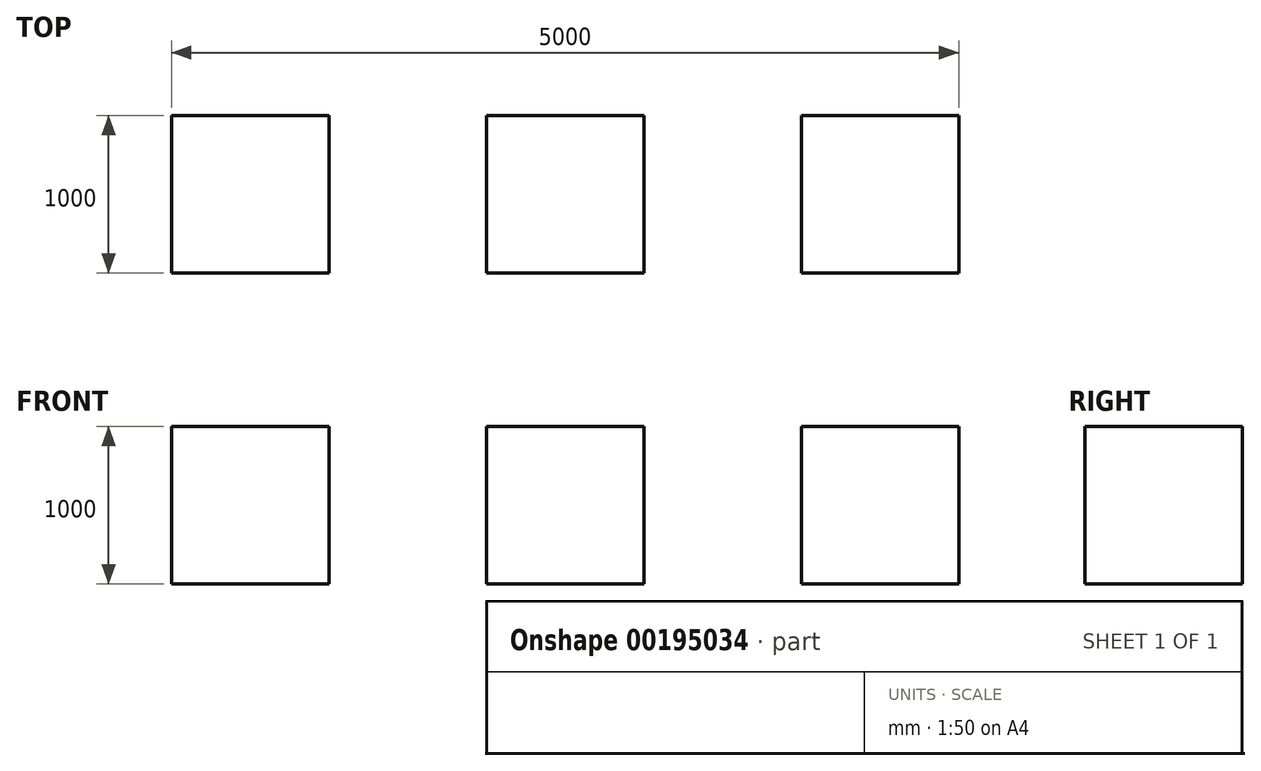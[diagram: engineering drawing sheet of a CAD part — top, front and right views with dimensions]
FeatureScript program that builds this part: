
annotation { "Feature Type Name" : "Feature", "Feature Type Description" : "" }
export const myFeature = defineFeature(function(context is Context, id is Id, definition is map)
    precondition{}
    {
        {
            var Q0;
            Q0=qCreatedBy(makeId("Top.planeOp"),FACE);
            var sketch = newSketch(context, id + "F0", { "sketchPlane" : qUnion([Q0])});
            skLineSegment(sketch, "E0.bottom", {"start": v(500, 500) * mm, "end": v(-500, 500) * mm});
            skLineSegment(sketch, "E0.top", {"start": v(500, -500) * mm, "end": v(-500, -500) * mm});
            skLineSegment(sketch, "E0.left", {"start": v(500, 500) * mm, "end": v(500, -500) * mm});
            skLineSegment(sketch, "E0.right", {"start": v(-500, 500) * mm, "end": v(-500, -500) * mm});
            skPoint(sketch, "E0.middle", {"position": v(0, 0) * mm});
            skSolve(sketch);
        }
        {
            var Q0;
            Q0 = qSketchRegion(id + "F0", true);
            extrude(context, id + "F1", {"entities" : qUnion([Q0]), "endBound" : BoundingType.SYMMETRIC, "depth" : 1000 * mm});
        }
        {
            var Q0;
            Q0=makeQuery(id+"F1.opExtrude","SWEPT_BODY",BODY,{"disambiguationData":[OSD([sQuery(id+"F0.wireOp",EDGE,"E0.bottom"),sQuery(id+"F0.wireOp",EDGE,"E0.top"),sQuery(id+"F0.wireOp",EDGE,"E0.left"),sQuery(id+"F0.wireOp",EDGE,"E0.right")])]});
            transform(context, id + "F2", {"entities" : qUnion([Q0]), "transformType" : TransformType.TRANSLATION_3D, "dx" : 2000 * mm, "dy" : 0 * mm, "dz" : 0 * mm, "makeCopy" : true});
        }
        {
            var Q0;
            Q0=makeQuery(id+"F2.opPattern","COPY",BODY,{"derivedFrom":makeQuery(id+"F1.opExtrude","SWEPT_BODY",BODY,{"disambiguationData":[OSD([sQuery(id+"F0.wireOp",EDGE,"E0.bottom"),sQuery(id+"F0.wireOp",EDGE,"E0.top"),sQuery(id+"F0.wireOp",EDGE,"E0.left"),sQuery(id+"F0.wireOp",EDGE,"E0.right")])]}),"instanceName":"1"});
            transform(context, id + "F3", {"entities" : qUnion([Q0]), "transformType" : TransformType.TRANSLATION_3D, "dx" : 2000 * mm, "dy" : 0 * mm, "dz" : 0 * mm, "makeCopy" : true});
        }
    });
